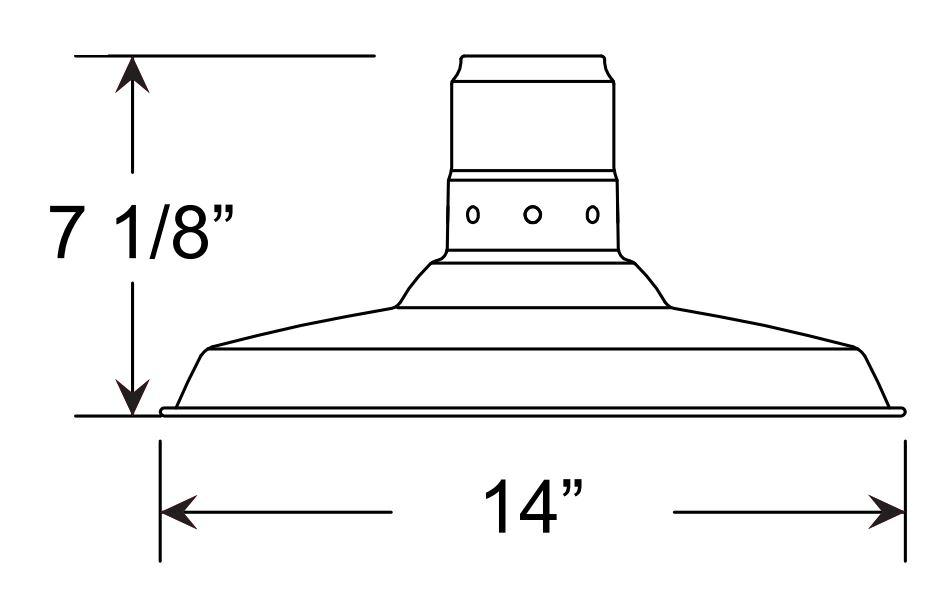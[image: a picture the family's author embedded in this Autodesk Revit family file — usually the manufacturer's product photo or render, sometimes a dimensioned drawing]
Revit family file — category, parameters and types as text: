
# Revit family: Tapered Dome_LED
name_source: partatom
category: Lighting Fixtures
units: mm (PartAtom-declared; Revit-internal decimal feet)

## family parameters
Always vertical = Yes
Cut with Voids When Loaded = No
Light Source = Yes
OmniClass Number = 23.80.70.00
OmniClass Title = Lighting
Part Type = Normal
Room Calculation Point = No
Round Connector Dimension = Use Diameter
Shared = No
Work Plane-Based = No

## types (6) — shared parameters
Body Colour = Spun aluminium
Body Material = body
Bulb = Light
CRI = >90
Color Filter = 16777215
Construction Material = Heavy Duty spun aluminum.
Default Elevation = 0' - 0"
Description = 120-277 Voltage
Dimming = 1%
Dimming Lamp Color Temperature Shift = <None>
Efficiency = 97-125 lumens per watt
Inside body material = Inside Body
Lamp = LED
Life = L70 50,000 hours
Load Classification = Lighting
Manufacturer = ANP Lighting
Photometric Web File = generic.ies
Power Factor = 1
Tilt Angle = 90.00°
URL = https://www.anplighting.com
Voltage = 277 V
Warranty = 5 year limited warranty

## per-type parameters (varying)
| type | Apparent Load | Fixture Diameter | Fixture Height | TD10 | TD12 | TD14 | TD16 | TD20 | TD24 | Wattage Comments | Weight |
| TD10 | 10 VA | 0' - 10" | 0' - 6" | Yes | No | No | No | No | No | 10W | 1.3 lb |
| TD12 | 16 VA | 1' - 0" | 0' - 7" | No | Yes | No | No | No | No | 16W | 1.9 lb |
| TD14 | 16 VA | 1' - 2" | 0' - 8" | No | No | Yes | No | No | No | 16W | 2.6 lb |
| TD16 | 24 VA | 1' - 4" | 0' - 9 1/2" | No | No | No | Yes | No | No | 24W | 3.4 lb |
| TD20 | 24 VA | 1' - 8" | 0' - 11 1/2" | No | No | No | No | Yes | No | 24W | 5.3 lb |
| TD24 | 37 VA | 2' - 0" | 1' - 2" | No | No | No | No | No | Yes | 37W | 7.7 lb |

note: column(s) folded — value = type name in every type: Model

## geometry (parser evidence)
native form markers: Sweep x45
no freeform markers — native parametric forms only
